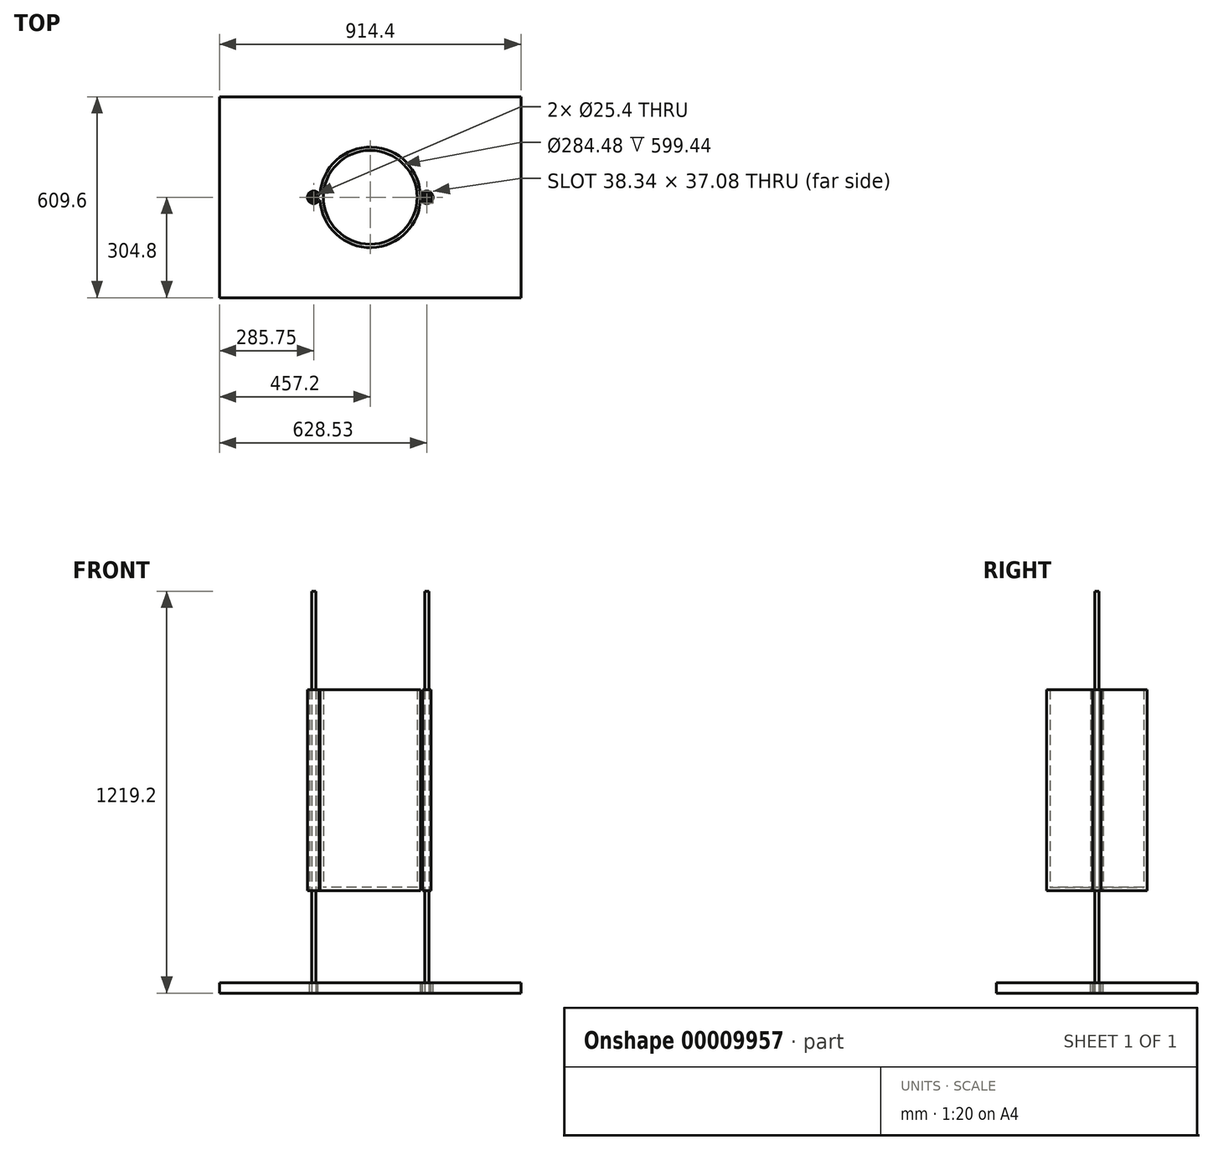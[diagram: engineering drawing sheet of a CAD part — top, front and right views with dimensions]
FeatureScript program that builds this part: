
annotation { "Feature Type Name" : "Feature", "Feature Type Description" : "" }
export const myFeature = defineFeature(function(context is Context, id is Id, definition is map)
    precondition{}
    {
        {
            var Q0;
            Q0=qCreatedBy(makeId("Top.planeOp"),FACE);
            var sketch = newSketch(context, id + "F0", { "sketchPlane" : qUnion([Q0])});
            skLineSegment(sketch, "E0", {"start": v(-457.2, 0) * mm, "end": v(457.2, 0) * mm, "construction": true});
            skLineSegment(sketch, "E1", {"start": v(0, 304.8) * mm, "end": v(0, -304.8) * mm, "construction": true});
            skLineSegment(sketch, "E2.bottom", {"start": v(-457.2, 304.8) * mm, "end": v(457.2, 304.8) * mm});
            skLineSegment(sketch, "E2.top", {"start": v(-457.2, -304.8) * mm, "end": v(457.2, -304.8) * mm});
            skLineSegment(sketch, "E2.left", {"start": v(-457.2, 304.8) * mm, "end": v(-457.2, -304.8) * mm});
            skLineSegment(sketch, "E2.right", {"start": v(457.2, 304.8) * mm, "end": v(457.2, -304.8) * mm});
            skCircle(sketch, "E3", {"center": v(0, 0) * mm, "radius": 152.4 * mm});
            skCircle(sketch, "E4", {"center": v(-171.45, 0) * mm, "radius": 12.7 * mm});
            skCircle(sketch, "E5.0.MirrorC", {"center": v(171.45, 0) * mm, "radius": 12.7 * mm});
            skCircle(sketch, "E6", {"center": v(-171.45, 0) * mm, "radius": 19.05 * mm});
            skCircle(sketch, "E7", {"center": v(171.45, 0) * mm, "radius": 19.05 * mm});
            skLineSegment(sketch, "E8", {"start": v(152.16, 8.54) * mm, "end": v(154.42, 8.54) * mm});
            skLineSegment(sketch, "E9.0.MirrorCS", {"start": v(152.16, -8.54) * mm, "end": v(154.42, -8.54) * mm});
            skLineSegment(sketch, "E10.0.MirrorCS", {"start": v(-152.16, -8.54) * mm, "end": v(-154.42, -8.54) * mm});
            skLineSegment(sketch, "E10.1.MirrorCS", {"start": v(-152.16, 8.54) * mm, "end": v(-154.42, 8.54) * mm});
            skSolve(sketch);
        }
        {
            var Q0;
            Q0=makeQuery(id+"F0.imprint","IMPRINT",FACE,{"disambiguationData":[TD([[makeQuery(id+"F0.imprint","IMPRINT",EDGE,{"derivedFrom":sQuery(id+"F0.wireOp",EDGE,"E2.bottom")}),-1.0]])]});
            var Q1;
            Q1=makeQuery(id+"F0.imprint","IMPRINT",FACE,{"disambiguationData":[TD([[makeQuery(id+"F0.imprint","IMPRINT",EDGE,{"derivedFrom":sQuery(id+"F0.wireOp",EDGE,"E3")}),1.0]])]});
            var Q2;
            Q2=makeQuery(id+"F0.imprint","IMPRINT",FACE,{"disambiguationData":[TD([[makeQuery(id+"F0.imprint","IMPRINT",EDGE,{"derivedFrom":sQuery(id+"F0.wireOp",EDGE,"E5.0.MirrorC")}),1.0]])]});
            var Q3;
            Q3=makeQuery(id+"F0.imprint","IMPRINT",FACE,{"disambiguationData":[TD([[makeQuery(id+"F0.imprint","IMPRINT",EDGE,{"derivedFrom":sQuery(id+"F0.wireOp",EDGE,"E4")}),-1.0]])]});
            var Q4;
            {var subQ0=sQuery(id+"F0.wireOp",EDGE,"E10.1.MirrorCS");Q4=makeQuery(id+"F0.imprint","IMPRINT",FACE,{"disambiguationData":[TD([[makeQuery(id+"F0.imprint","IMPRINT",EDGE,{"derivedFrom":subQ0}),1.0]])]});}
            var Q5;
            {var subQ0=sQuery(id+"F0.wireOp",EDGE,"E10.0.MirrorCS");Q5=makeQuery(id+"F0.imprint","IMPRINT",FACE,{"disambiguationData":[TD([[makeQuery(id+"F0.imprint","IMPRINT",EDGE,{"derivedFrom":subQ0}),-1.0]])]});}
            var Q6;
            {var subQ0=sQuery(id+"F0.wireOp",EDGE,"E9.0.MirrorCS");Q6=makeQuery(id+"F0.imprint","IMPRINT",FACE,{"disambiguationData":[TD([[makeQuery(id+"F0.imprint","IMPRINT",EDGE,{"derivedFrom":subQ0}),1.0]])]});}
            var Q7;
            {var subQ0=sQuery(id+"F0.wireOp",EDGE,"E8");Q7=makeQuery(id+"F0.imprint","IMPRINT",FACE,{"disambiguationData":[TD([[makeQuery(id+"F0.imprint","IMPRINT",EDGE,{"derivedFrom":subQ0}),-1.0]])]});}
            extrude(context, id + "F1", {"entities" : qUnion([Q0, Q1, Q2, Q3, Q4, Q5, Q6, Q7]), "oppositeDirection" : true, "depth" : 31.75 * mm});
        }
        {
            var Q0;
            Q0=makeQuery(id+"F0.imprint","IMPRINT",FACE,{"disambiguationData":[TD([[makeQuery(id+"F0.imprint","IMPRINT",EDGE,{"derivedFrom":sQuery(id+"F0.wireOp",EDGE,"E3")}),1.0]])]});
            var Q1;
            Q1=makeQuery(id+"F0.imprint","IMPRINT",FACE,{"disambiguationData":[TD([[makeQuery(id+"F0.imprint","IMPRINT",EDGE,{"derivedFrom":sQuery(id+"F0.wireOp",EDGE,"E5.0.MirrorC")}),1.0]])]});
            var Q2;
            Q2=makeQuery(id+"F0.imprint","IMPRINT",FACE,{"disambiguationData":[TD([[makeQuery(id+"F0.imprint","IMPRINT",EDGE,{"derivedFrom":sQuery(id+"F0.wireOp",EDGE,"E4")}),-1.0]])]});
            var Q3;
            {var subQ0=sQuery(id+"F0.wireOp",EDGE,"E9.0.MirrorCS");Q3=makeQuery(id+"F0.imprint","IMPRINT",FACE,{"disambiguationData":[TD([[makeQuery(id+"F0.imprint","IMPRINT",EDGE,{"derivedFrom":subQ0}),1.0]])]});}
            var Q4;
            {var subQ0=sQuery(id+"F0.wireOp",EDGE,"E8");Q4=makeQuery(id+"F0.imprint","IMPRINT",FACE,{"disambiguationData":[TD([[makeQuery(id+"F0.imprint","IMPRINT",EDGE,{"derivedFrom":subQ0}),-1.0]])]});}
            var Q5;
            {var subQ0=sQuery(id+"F0.wireOp",EDGE,"E10.1.MirrorCS");Q5=makeQuery(id+"F0.imprint","IMPRINT",FACE,{"disambiguationData":[TD([[makeQuery(id+"F0.imprint","IMPRINT",EDGE,{"derivedFrom":subQ0}),1.0]])]});}
            var Q6;
            {var subQ0=sQuery(id+"F0.wireOp",EDGE,"E10.0.MirrorCS");Q6=makeQuery(id+"F0.imprint","IMPRINT",FACE,{"disambiguationData":[TD([[makeQuery(id+"F0.imprint","IMPRINT",EDGE,{"derivedFrom":subQ0}),-1.0]])]});}
            extrude(context, id + "F2", {"entities" : qUnion([Q0, Q1, Q2, Q3, Q4, Q5, Q6]), "depth" : 889 * mm, "hasSecondDirection" : true, "secondDirectionOppositeDirection" : false, "secondDirectionDepth" : 279.4 * mm});
        }
        {
            var Q0;
            Q0=makeQuery(id+"F2.opExtrude","CAP_FACE",FACE,{"disambiguationData":[OSD([sQuery(id+"F0.wireOp",EDGE,"E3"),sQuery(id+"F0.wireOp",EDGE,"E4"),sQuery(id+"F0.wireOp",EDGE,"E5.0.MirrorC"),sQuery(id+"F0.wireOp",EDGE,"E6"),sQuery(id+"F0.wireOp",EDGE,"E7"),sQuery(id+"F0.wireOp",EDGE,"E9.0.MirrorCS"),sQuery(id+"F0.wireOp",EDGE,"E8"),sQuery(id+"F0.wireOp",EDGE,"E10.0.MirrorCS"),sQuery(id+"F0.wireOp",EDGE,"E10.1.MirrorCS")])],"isStart":false});
            shell(context, id + "F3", {"entities" : qUnion([Q0]), "thickness" : 10.16 * mm});
        }
        {
            var Q0;
            Q0=makeQuery(id+"F1.opExtrude","CAP_FACE",FACE,{"disambiguationData":[OSD([sQuery(id+"F0.wireOp",EDGE,"E2.bottom"),sQuery(id+"F0.wireOp",EDGE,"E2.top"),sQuery(id+"F0.wireOp",EDGE,"E2.left"),sQuery(id+"F0.wireOp",EDGE,"E2.right"),sQuery(id+"F0.wireOp",EDGE,"E4"),sQuery(id+"F0.wireOp",EDGE,"E5.0.MirrorC")])],"isStart":false});
            var sketch = newSketch(context, id + "F4", { "sketchPlane" : qUnion([Q0])});
            skCircle(sketch, "E11", {"center": v(171.45, 0) * mm, "radius": 6.35 * mm});
            skCircle(sketch, "E12", {"center": v(-171.45, 0) * mm, "radius": 6.35 * mm});
            skSolve(sketch);
        }
        {
            var Q0;
            Q0=makeQuery(id+"F4.imprint","IMPRINT",FACE,{"disambiguationData":[TD([[makeQuery(id+"F4.imprint","IMPRINT",EDGE,{"derivedFrom":sQuery(id+"F4.wireOp",EDGE,"E11")}),1.0]])]});
            var Q1;
            Q1=makeQuery(id+"F4.imprint","IMPRINT",FACE,{"disambiguationData":[TD([[makeQuery(id+"F4.imprint","IMPRINT",EDGE,{"derivedFrom":sQuery(id+"F4.wireOp",EDGE,"E12")}),1.0]])]});
            extrude(context, id + "F5", {"entities" : qUnion([Q0, Q1]), "oppositeDirection" : true, "depth" : 1219.2 * mm});
        }
    });
